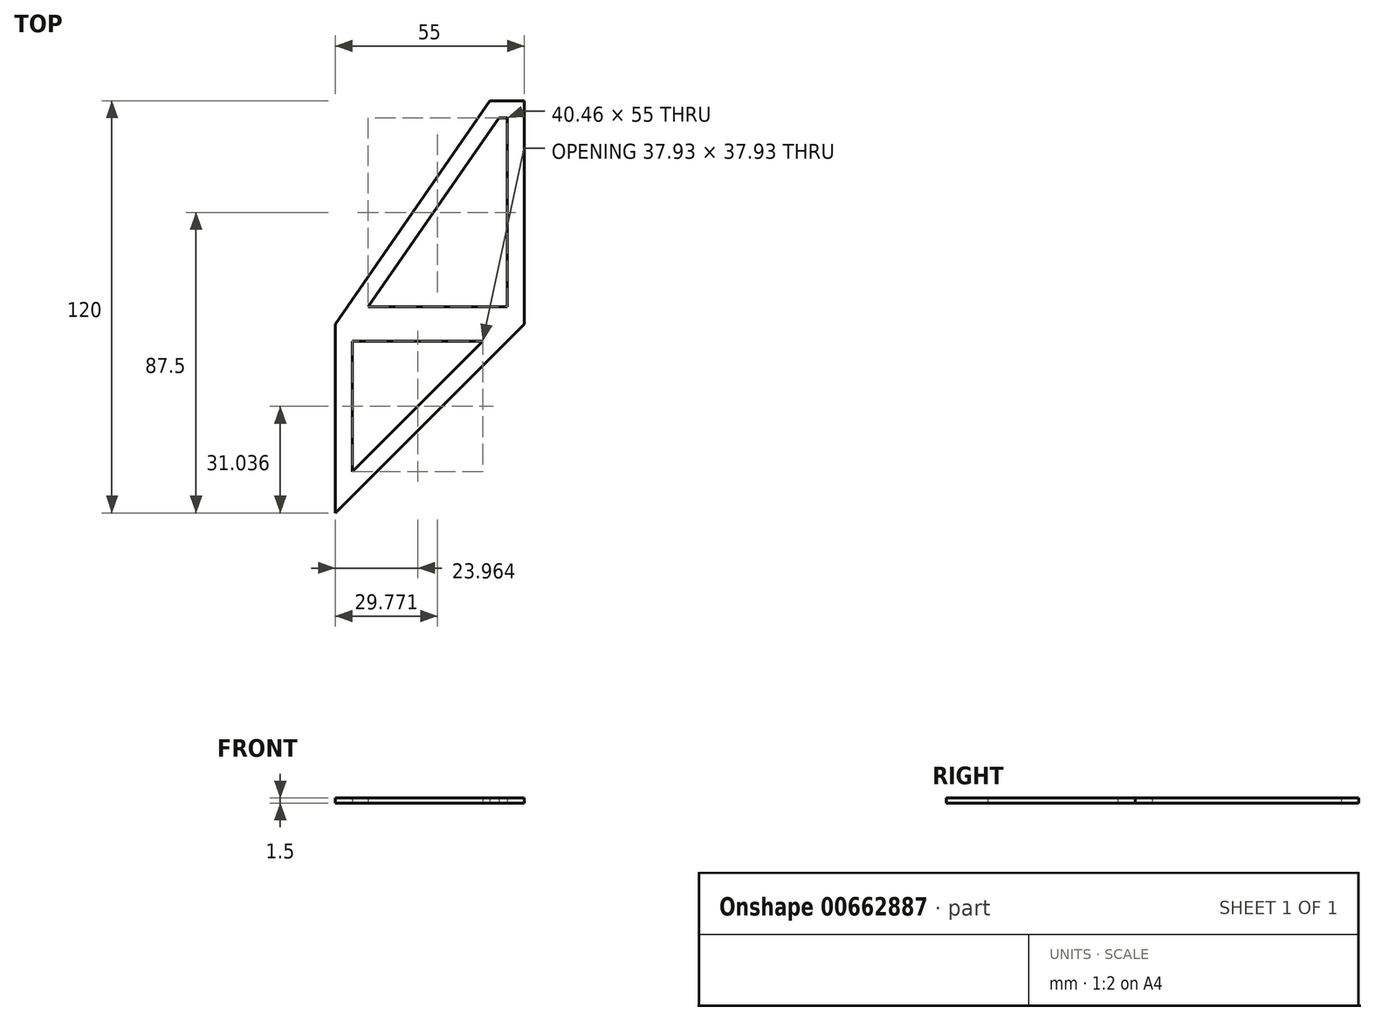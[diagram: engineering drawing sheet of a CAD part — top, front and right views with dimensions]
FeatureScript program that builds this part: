
annotation { "Feature Type Name" : "Feature", "Feature Type Description" : "" }
export const myFeature = defineFeature(function(context is Context, id is Id, definition is map)
    precondition{}
    {
        {
            var Q0;
            Q0=qCreatedBy(makeId("Top.planeOp"),FACE);
            var sketch = newSketch(context, id + "F0", { "sketchPlane" : qUnion([Q0])});
            skLineSegment(sketch, "E0", {"start": v(0, 0) * mm, "end": v(55, 0) * mm});
            skLineSegment(sketch, "E1", {"start": v(55, 0) * mm, "end": v(55, 65) * mm});
            skLineSegment(sketch, "E2", {"start": v(55, 65) * mm, "end": v(45, 65) * mm});
            skLineSegment(sketch, "E3", {"start": v(45, 65) * mm, "end": v(0, 0) * mm});
            skLineSegment(sketch, "E4", {"start": v(0, -55) * mm, "end": v(55, 0) * mm});
            skLineSegment(sketch, "E5", {"start": v(0, 0) * mm, "end": v(0, -55) * mm});
            skLineSegment(sketch, "E6.0", {"start": v(5, -5) * mm, "end": v(5, -42.93) * mm});
            skLineSegment(sketch, "E6.1", {"start": v(5, -5) * mm, "end": v(42.93, -5) * mm});
            skLineSegment(sketch, "E6.2", {"start": v(5, -42.93) * mm, "end": v(42.93, -5) * mm});
            skLineSegment(sketch, "E7.0", {"start": v(47.62, 60) * mm, "end": v(9.54, 5) * mm});
            skLineSegment(sketch, "E7.1", {"start": v(50, 60) * mm, "end": v(47.62, 60) * mm});
            skLineSegment(sketch, "E7.2", {"start": v(50, 5) * mm, "end": v(50, 60) * mm});
            skLineSegment(sketch, "E7.3", {"start": v(9.54, 5) * mm, "end": v(50, 5) * mm});
            skSolve(sketch);
        }
        {
            var Q0;
            Q0=makeQuery(id+"F0.imprint","IMPRINT",FACE,{"disambiguationData":[TD([[makeQuery(id+"F0.imprint","IMPRINT",EDGE,{"derivedFrom":sQuery(id+"F0.wireOp",EDGE,"E0")}),1.0]])]});
            var Q1;
            Q1=makeQuery(id+"F0.imprint","IMPRINT",FACE,{"disambiguationData":[TD([[makeQuery(id+"F0.imprint","IMPRINT",EDGE,{"derivedFrom":sQuery(id+"F0.wireOp",EDGE,"E0")}),-1.0]])]});
            extrude(context, id + "F1", {"entities" : qUnion([Q0, Q1]), "depth" : 1.5 * mm, "offsetDistance" : 25 * mm});
        }
    });
